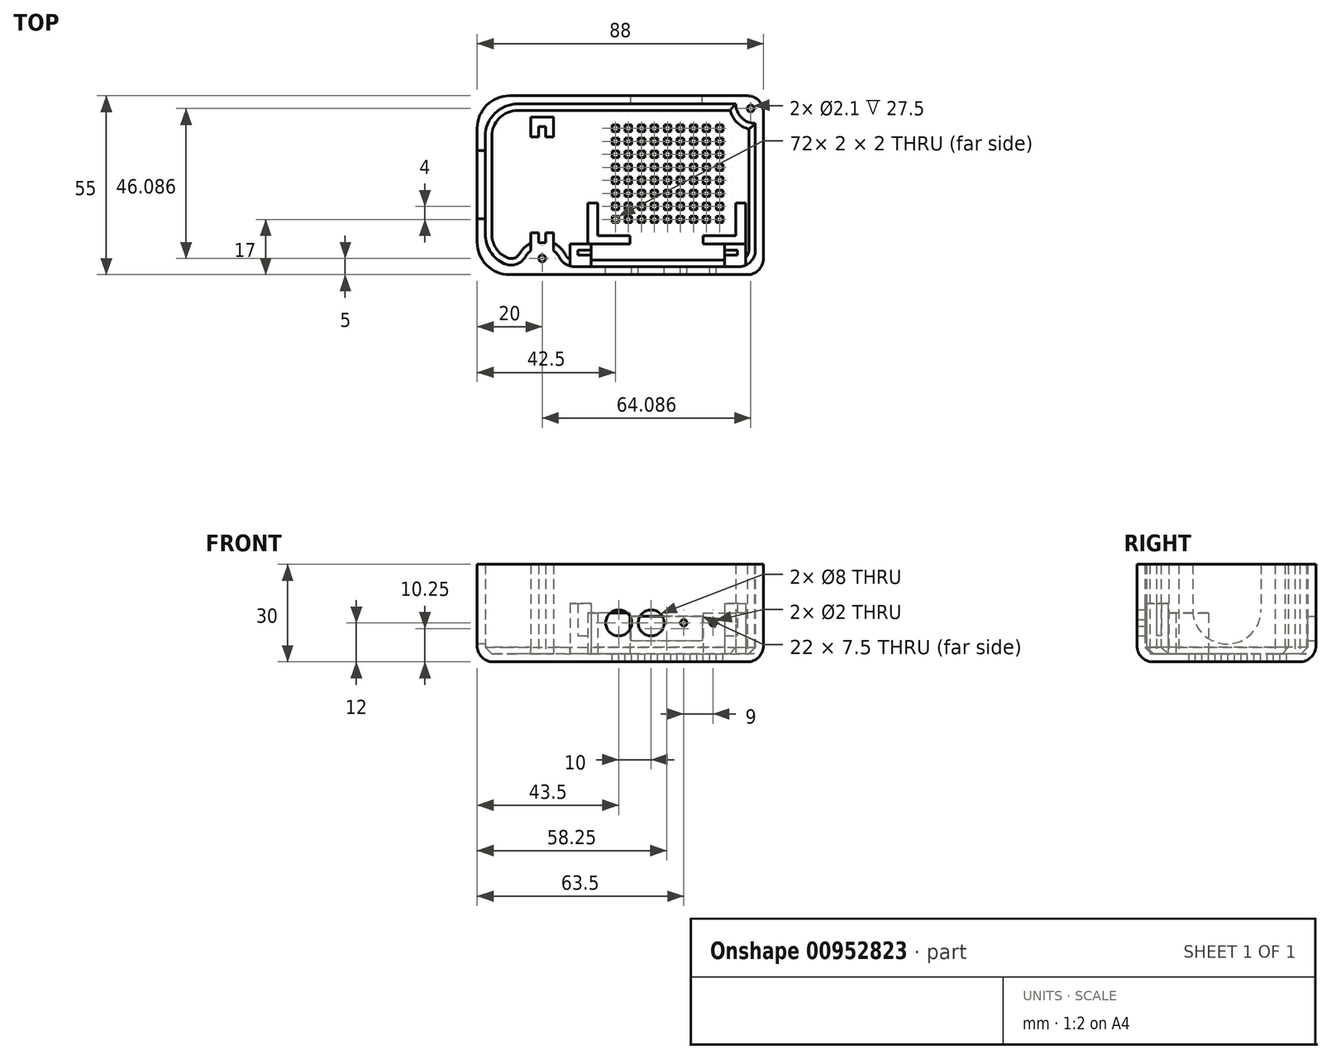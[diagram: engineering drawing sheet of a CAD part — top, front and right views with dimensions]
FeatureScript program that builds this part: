
annotation { "Feature Type Name" : "Feature", "Feature Type Description" : "" }
export const myFeature = defineFeature(function(context is Context, id is Id, definition is map)
    precondition{}
    {
        {
            var Q0;
            Q0=qCreatedBy(makeId("Top.planeOp"),FACE);
            var sketch = newSketch(context, id + "F0", { "sketchPlane" : qUnion([Q0])});
            skLineSegment(sketch, "E0", {"start": v(-88, 0) * mm, "end": v(0, 0) * mm});
            skLineSegment(sketch, "E1", {"start": v(0, 0) * mm, "end": v(0, -55) * mm});
            skLineSegment(sketch, "E2", {"start": v(0, -55) * mm, "end": v(-88, -55) * mm});
            skLineSegment(sketch, "E3", {"start": v(-88, -55) * mm, "end": v(-88, 0) * mm});
            skLineSegment(sketch, "E4", {"start": v(-85.5, -52.5) * mm, "end": v(-85.5, -2.5) * mm});
            skLineSegment(sketch, "E5", {"start": v(-71.5, -12.6) * mm, "end": v(-71.5, -6.5) * mm});
            skLineSegment(sketch, "E6", {"start": v(-64.5, -6.5) * mm, "end": v(-64.5, -12.6) * mm});
            skLineSegment(sketch, "E7", {"start": v(-64.5, -12.6) * mm, "end": v(-66.95, -12.6) * mm});
            skLineSegment(sketch, "E8", {"start": v(-66.95, -12.6) * mm, "end": v(-66.95, -9.5) * mm});
            skLineSegment(sketch, "E9", {"start": v(-66.95, -9.5) * mm, "end": v(-69.05, -9.5) * mm});
            skLineSegment(sketch, "E10", {"start": v(-69.05, -9.5) * mm, "end": v(-69.05, -12.6) * mm});
            skLineSegment(sketch, "E11", {"start": v(-69.05, -12.6) * mm, "end": v(-71.5, -12.6) * mm});
            skLineSegment(sketch, "E12", {"start": v(-93.85, -27.35) * mm, "end": v(11.82, -27.35) * mm, "construction": true});
            skLineSegment(sketch, "E13.MirrorCS", {"start": v(-69.05, -42.1) * mm, "end": v(-71.5, -42.1) * mm});
            skLineSegment(sketch, "E14.MirrorCS", {"start": v(-66.95, -42.1) * mm, "end": v(-66.95, -45.2) * mm});
            skLineSegment(sketch, "E15.MirrorCS", {"start": v(-71.5, -42.1) * mm, "end": v(-71.5, -47.63) * mm});
            skLineSegment(sketch, "E16.MirrorCS", {"start": v(-69.05, -45.2) * mm, "end": v(-69.05, -42.1) * mm});
            skLineSegment(sketch, "E17.MirrorCS", {"start": v(-66.95, -45.2) * mm, "end": v(-69.05, -45.2) * mm});
            skLineSegment(sketch, "E18.MirrorCS", {"start": v(-64.5, -42.1) * mm, "end": v(-66.95, -42.1) * mm});
            skLineSegment(sketch, "E19", {"start": v(-85.5, -52.5) * mm, "end": v(-2.5, -52.5) * mm});
            skLineSegment(sketch, "E20", {"start": v(-71.5, -6.5) * mm, "end": v(-64.5, -6.5) * mm});
            skArc(sketch, "E21", {"start": v(-8.5, -2.5) * mm, "mid": v(-6.74, -6.74) * mm, "end": v(-2.5, -8.5) * mm});
            skArc(sketch, "E22", {"start": v(-74, -52.5) * mm, "mid": v(-73.34, -49.76) * mm, "end": v(-71.5, -47.63) * mm});
            skLineSegment(sketch, "E23", {"start": v(-64.5, -47.82) * mm, "end": v(-64.5, -47.82) * mm});
            skLineSegment(sketch, "E24", {"start": v(-64.5, -47.82) * mm, "end": v(-64.5, -42.1) * mm});
            skArc(sketch, "E25", {"start": v(-64.5, -47.63) * mm, "mid": v(-62.66, -49.76) * mm, "end": v(-62, -52.5) * mm});
            skLineSegment(sketch, "E26", {"start": v(-8.5, -2.5) * mm, "end": v(-85.5, -2.5) * mm});
            skLineSegment(sketch, "E27", {"start": v(-2.5, -8.5) * mm, "end": v(-2.5, -52.5) * mm});
            skLineSegment(sketch, "E28", {"start": v(-68, -52.5) * mm, "end": v(-68, -38.94) * mm, "construction": true});
            skCircle(sketch, "E29", {"center": v(-68, -50) * mm, "radius": 1.05 * mm});
            skLineSegment(sketch, "E30", {"start": v(-2.5, -2.5) * mm, "end": v(-3.91, -3.91) * mm, "construction": true});
            skLineSegment(sketch, "E31", {"start": v(-3.91, -3.91) * mm, "end": v(-2.5, -5.33) * mm, "construction": true});
            skCircle(sketch, "E32", {"center": v(-3.91, -3.91) * mm, "radius": 1.05 * mm});
            skSolve(sketch);
        }
        {
            var Q0;
            Q0=qCreatedBy(makeId("Top.planeOp"),FACE);
            var sketch = newSketch(context, id + "F1", { "sketchPlane" : qUnion([Q0])});
            skPoint(sketch, "E33.middle", {"position": v(0, 0) * mm});
            skLineSegment(sketch, "E34.bottom", {"start": v(0, 0) * mm, "end": v(-88, 0) * mm});
            skLineSegment(sketch, "E34.top", {"start": v(0, -55) * mm, "end": v(-88, -55) * mm});
            skLineSegment(sketch, "E34.left", {"start": v(0, 0) * mm, "end": v(0, -55) * mm});
            skLineSegment(sketch, "E34.right", {"start": v(-88, 0) * mm, "end": v(-88, -55) * mm});
            skSolve(sketch);
        }
        {
            var Q0;
            Q0=qCreatedBy(makeId("Top.planeOp"),FACE);
            var sketch = newSketch(context, id + "F2", { "sketchPlane" : qUnion([Q0])});
            skLineSegment(sketch, "E35", {"start": v(-5.5, -33) * mm, "end": v(-8.5, -33) * mm});
            skLineSegment(sketch, "E36", {"start": v(-8.5, -33) * mm, "end": v(-8.5, -43) * mm});
            skLineSegment(sketch, "E37", {"start": v(-18.5, -43) * mm, "end": v(-8.5, -43) * mm});
            skLineSegment(sketch, "E38", {"start": v(-18.5, -43) * mm, "end": v(-18.5, -45.5) * mm});
            skLineSegment(sketch, "E39", {"start": v(-18.5, -45.5) * mm, "end": v(-5.5, -45.5) * mm});
            skLineSegment(sketch, "E40", {"start": v(-5.5, -45.5) * mm, "end": v(-5.5, -33) * mm});
            skLineSegment(sketch, "E41", {"start": v(-29.75, -52.22) * mm, "end": v(-29.75, 32.06) * mm, "construction": true});
            skLineSegment(sketch, "E42.MirrorCS", {"start": v(-54, -33) * mm, "end": v(-51, -33) * mm});
            skLineSegment(sketch, "E43.MirrorCS", {"start": v(-41, -43) * mm, "end": v(-41, -45.5) * mm});
            skLineSegment(sketch, "E44.MirrorCS", {"start": v(-51, -33) * mm, "end": v(-51, -43) * mm});
            skLineSegment(sketch, "E45.MirrorCS", {"start": v(-41, -45.5) * mm, "end": v(-54, -45.5) * mm});
            skLineSegment(sketch, "E46.MirrorCS", {"start": v(-54, -45.5) * mm, "end": v(-54, -33) * mm});
            skLineSegment(sketch, "E47.MirrorCS", {"start": v(-41, -43) * mm, "end": v(-51, -43) * mm});
            skSolve(sketch);
        }
        {
            var Q0;
            Q0=qCreatedBy(makeId("Top.planeOp"),FACE);
            var sketch = newSketch(context, id + "F3", { "sketchPlane" : qUnion([Q0])});
            skLineSegment(sketch, "E48", {"start": v(-32.5, -56.28) * mm, "end": v(-32.5, -44.7) * mm, "construction": true});
            skLineSegment(sketch, "E49", {"start": v(-12, -45.5) * mm, "end": v(-5.5, -45.5) * mm});
            skLineSegment(sketch, "E50", {"start": v(-12, -52.5) * mm, "end": v(-5.5, -52.5) * mm});
            skLineSegment(sketch, "E51", {"start": v(-12, -45.5) * mm, "end": v(-12, -52.5) * mm});
            skLineSegment(sketch, "E52.MirrorCS", {"start": v(-53, -45.5) * mm, "end": v(-53, -52.5) * mm});
            skLineSegment(sketch, "E53.MirrorCS", {"start": v(-53, -45.5) * mm, "end": v(-59.5, -45.5) * mm});
            skPoint(sketch, "E54", {"position": v(-5.5, -45.5) * mm});
            skPoint(sketch, "E55", {"position": v(-5.5, -52.5) * mm});
            skLineSegment(sketch, "E56", {"start": v(-5.5, -45.5) * mm, "end": v(-5.5, -52.5) * mm});
            skLineSegment(sketch, "E57", {"start": v(-5.5, -52.5) * mm, "end": v(-5.5, -52.5) * mm});
            skLineSegment(sketch, "E58.MirrorCS", {"start": v(-59.5, -45.5) * mm, "end": v(-59.5, -52.5) * mm});
            skLineSegment(sketch, "E59.MirrorCS", {"start": v(-53, -52.5) * mm, "end": v(-59.5, -52.5) * mm});
            skSolve(sketch);
        }
        {
            var Q0;
            Q0=qCreatedBy(makeId("Top.planeOp"),FACE);
            var sketch = newSketch(context, id + "F4", { "sketchPlane" : qUnion([Q0])});
            skLineSegment(sketch, "E60", {"start": v(-12, -52.5) * mm, "end": v(-12, -49) * mm});
            skLineSegment(sketch, "E61", {"start": v(-12, -49) * mm, "end": v(-8, -49) * mm});
            skLineSegment(sketch, "E62", {"start": v(-8, -49) * mm, "end": v(-8, -47.5) * mm});
            skLineSegment(sketch, "E63", {"start": v(-8, -47.5) * mm, "end": v(-12, -47.5) * mm});
            skLineSegment(sketch, "E64", {"start": v(-12, -47.5) * mm, "end": v(-12, -45.5) * mm});
            skLineSegment(sketch, "E65", {"start": v(-32.5, -55) * mm, "end": v(-32.5, -43.43) * mm, "construction": true});
            skLineSegment(sketch, "E66", {"start": v(-12, -45.5) * mm, "end": v(-5.5, -45.5) * mm});
            skLineSegment(sketch, "E67.MirrorCS", {"start": v(-57, -49) * mm, "end": v(-57, -47.5) * mm});
            skLineSegment(sketch, "E68.MirrorCS", {"start": v(-53, -52.5) * mm, "end": v(-53, -49) * mm});
            skLineSegment(sketch, "E69.MirrorCS", {"start": v(-57, -47.5) * mm, "end": v(-53, -47.5) * mm});
            skLineSegment(sketch, "E70.MirrorCS", {"start": v(-59.5, -52.5) * mm, "end": v(-53, -52.5) * mm});
            skLineSegment(sketch, "E71.MirrorCS", {"start": v(-53, -47.5) * mm, "end": v(-53, -45.5) * mm});
            skLineSegment(sketch, "E72.MirrorCS", {"start": v(-53, -49) * mm, "end": v(-57, -49) * mm});
            skLineSegment(sketch, "E73.MirrorCS", {"start": v(-53, -45.5) * mm, "end": v(-59.5, -45.5) * mm});
            skLineSegment(sketch, "E74", {"start": v(-5.5, -45.5) * mm, "end": v(-5.5, -52.5) * mm});
            skLineSegment(sketch, "E75", {"start": v(-5.5, -52.5) * mm, "end": v(-5.5, -52.5) * mm});
            skLineSegment(sketch, "E76", {"start": v(-5.5, -52.5) * mm, "end": v(-12, -52.5) * mm});
            skLineSegment(sketch, "E77.MirrorCS", {"start": v(21.5, -55) * mm, "end": v(21.5, -43.43) * mm, "construction": true});
            skLineSegment(sketch, "E78.MirrorCS", {"start": v(-59.5, -45.5) * mm, "end": v(-59.5, -52.5) * mm});
            skSolve(sketch);
        }
        {
            var Q0;
            Q0=makeQuery(id+"F0.imprint","IMPRINT",FACE,{"disambiguationData":[TD([[makeQuery(id+"F0.imprint","IMPRINT",EDGE,{"derivedFrom":sQuery(id+"F0.wireOp",EDGE,"E0")}),-1.0]])]});
            var Q1;
            Q1=makeQuery(id+"F0.imprint","IMPRINT",FACE,{"disambiguationData":[TD([[makeQuery(id+"F0.imprint","IMPRINT",EDGE,{"derivedFrom":sQuery(id+"F0.wireOp",EDGE,"E13.MirrorCS")}),1.0]])]});
            var Q2;
            Q2=makeQuery(id+"F0.imprint","IMPRINT",FACE,{"disambiguationData":[TD([[makeQuery(id+"F0.imprint","IMPRINT",EDGE,{"derivedFrom":sQuery(id+"F0.wireOp",EDGE,"E5")}),-1.0]])]});
            extrude(context, id + "F5", {"entities" : qUnion([Q0, Q1, Q2]), "depth" : 30 * mm, "offsetDistance" : 25 * mm});
        }
        {
            var Q0;
            Q0 = qSketchRegion(id + "F2", true);
            extrude(context, id + "F6", {"entities" : qUnion([Q0]), "depth" : 15 * mm, "offsetDistance" : 25 * mm});
        }
        {
            var Q0;
            Q0 = qSketchRegion(id + "F3", true);
            extrude(context, id + "F7", {"entities" : qUnion([Q0]), "operationType" : NewBodyOperationType.ADD, "depth" : 8 * mm, "offsetDistance" : 25 * mm});
        }
        {
            var Q0;
            Q0 = qSketchRegion(id + "F4", true);
            extrude(context, id + "F8", {"entities" : qUnion([Q0]), "operationType" : NewBodyOperationType.ADD, "depth" : 18 * mm, "offsetDistance" : 25 * mm});
        }
        {
            var Q0;
            Q0 = qSketchRegion(id + "F1", true);
            extrude(context, id + "F9", {"entities" : qUnion([Q0]), "depth" : 2.5 * mm, "offsetDistance" : 25 * mm});
        }
        {
            var Q0;
            Q0=makeQuery(id+"F5.opExtrude","SWEPT_BODY",BODY,{"disambiguationData":[OSD([sQuery(id+"F0.wireOp",EDGE,"E0"),sQuery(id+"F0.wireOp",EDGE,"E1"),sQuery(id+"F0.wireOp",EDGE,"E2"),sQuery(id+"F0.wireOp",EDGE,"E3"),sQuery(id+"F0.wireOp",EDGE,"UuoHDoxM-e8rz-IagH-wuba-yFCC0wOmhfrt"),sQuery(id+"F0.wireOp",EDGE,"E4"),sQuery(id+"F0.wireOp",EDGE,"E5"),sQuery(id+"F0.wireOp",EDGE,"E6"),sQuery(id+"F0.wireOp",EDGE,"E7"),sQuery(id+"F0.wireOp",EDGE,"E8"),sQuery(id+"F0.wireOp",EDGE,"E9"),sQuery(id+"F0.wireOp",EDGE,"E10"),sQuery(id+"F0.wireOp",EDGE,"E11"),sQuery(id+"F0.wireOp",EDGE,"c786309d-101e-4053-9150-d0af641cc12e"),sQuery(id+"F0.wireOp",EDGE,"E19"),sQuery(id+"F0.wireOp",EDGE,"HcqVvm8B-6W9z-mqu9-0GbS-zFuDXKySd18V")])]});
            var Q1;
            Q1=makeQuery(id+"F5.opExtrude","SWEPT_BODY",BODY,{"disambiguationData":[OSD([sQuery(id+"F0.wireOp",EDGE,"E13.MirrorCS"),sQuery(id+"F0.wireOp",EDGE,"E14.MirrorCS"),sQuery(id+"F0.wireOp",EDGE,"E15.MirrorCS"),sQuery(id+"F0.wireOp",EDGE,"064b8b4c-f276-4261-8800-d9a24fd23e0e3.MirrorCS"),sQuery(id+"F0.wireOp",EDGE,"E16.MirrorCS"),sQuery(id+"F0.wireOp",EDGE,"E17.MirrorCS"),sQuery(id+"F0.wireOp",EDGE,"E18.MirrorCS"),sQuery(id+"F0.wireOp",EDGE,"gorcFAZ2-i92h-ynGc-5GPt-G5OjvUxhf4RJ")])]});
            var Q2;
            Q2=makeQuery(id+"F6.opExtrude","SWEPT_BODY",BODY,{"disambiguationData":[OSD([sQuery(id+"F2.wireOp",EDGE,"fb9ec073-7efa-4419-bfd9-468364ba8700"),sQuery(id+"F2.wireOp",EDGE,"ed1e150d-128d-4553-bff4-cb28458386a2"),sQuery(id+"F2.wireOp",EDGE,"0a0392a0-6fd0-4df2-8425-dfe9aab30372"),sQuery(id+"F2.wireOp",EDGE,"c3ed98f8-111d-4dfb-8951-0a7b6b337b95"),sQuery(id+"F2.wireOp",EDGE,"ekVp80hc-O6ig-nOgL-KVfI-wofW4DGdbD3E"),sQuery(id+"F2.wireOp",EDGE,"EOFYb0tf-Urno-pUMQ-HgLK-OjDsxmRxz7sO")])]});
            var Q3;
            Q3=makeQuery(id+"F6.opExtrude","SWEPT_BODY",BODY,{"disambiguationData":[OSD([sQuery(id+"F2.wireOp",EDGE,"E35"),sQuery(id+"F2.wireOp",EDGE,"E36"),sQuery(id+"F2.wireOp",EDGE,"E37"),sQuery(id+"F2.wireOp",EDGE,"E38"),sQuery(id+"F2.wireOp",EDGE,"E39"),sQuery(id+"F2.wireOp",EDGE,"E40")])]});
            var Q4;
            Q4=makeQuery(id+"F9.opExtrude","SWEPT_BODY",BODY,{"disambiguationData":[OSD([sQuery(id+"F1.wireOp",EDGE,"E34.bottom"),sQuery(id+"F1.wireOp",EDGE,"E34.top"),sQuery(id+"F1.wireOp",EDGE,"E34.left"),sQuery(id+"F1.wireOp",EDGE,"E34.right")])]});
            var Q5;
            Q5=makeQuery(id+"F8.opExtrude","SWEPT_BODY",BODY,{"disambiguationData":[OSD([sQuery(id+"F4.wireOp",EDGE,"E60"),sQuery(id+"F4.wireOp",EDGE,"E61"),sQuery(id+"F4.wireOp",EDGE,"E62"),sQuery(id+"F4.wireOp",EDGE,"E63"),sQuery(id+"F4.wireOp",EDGE,"E64"),sQuery(id+"F4.wireOp",EDGE,"E66"),sQuery(id+"F4.wireOp",EDGE,"E74"),sQuery(id+"F4.wireOp",EDGE,"E76")])]});
            var Q6;
            Q6=makeQuery(id+"F8.opExtrude","SWEPT_BODY",BODY,{"disambiguationData":[OSD([sQuery(id+"F4.wireOp",EDGE,"E67.MirrorCS"),sQuery(id+"F4.wireOp",EDGE,"E68.MirrorCS"),sQuery(id+"F4.wireOp",EDGE,"E69.MirrorCS"),sQuery(id+"F4.wireOp",EDGE,"E70.MirrorCS"),sQuery(id+"F4.wireOp",EDGE,"E71.MirrorCS"),sQuery(id+"F4.wireOp",EDGE,"E72.MirrorCS"),sQuery(id+"F4.wireOp",EDGE,"E73.MirrorCS"),sQuery(id+"F4.wireOp",EDGE,"E78.MirrorCS")])]});
            var Q7;
            Q7=makeQuery(id+"F7.opExtrude","SWEPT_BODY",BODY,{"disambiguationData":[OSD([sQuery(id+"F3.wireOp",EDGE,"E49"),sQuery(id+"F3.wireOp",EDGE,"E50"),sQuery(id+"F3.wireOp",EDGE,"E51"),sQuery(id+"F3.wireOp",EDGE,"E56")])]});
            var Q8;
            Q8=makeQuery(id+"F7.opExtrude","SWEPT_BODY",BODY,{"disambiguationData":[OSD([sQuery(id+"F3.wireOp",EDGE,"E52.MirrorCS"),sQuery(id+"F3.wireOp",EDGE,"E53.MirrorCS"),sQuery(id+"F3.wireOp",EDGE,"E58.MirrorCS"),sQuery(id+"F3.wireOp",EDGE,"E59.MirrorCS")])]});
            var Q9;
            Q9=makeQuery(id+"F6.opExtrude","SWEPT_BODY",BODY,{"disambiguationData":[OSD([sQuery(id+"F2.wireOp",EDGE,"E42.MirrorCS"),sQuery(id+"F2.wireOp",EDGE,"E43.MirrorCS"),sQuery(id+"F2.wireOp",EDGE,"E44.MirrorCS"),sQuery(id+"F2.wireOp",EDGE,"E45.MirrorCS"),sQuery(id+"F2.wireOp",EDGE,"E46.MirrorCS"),sQuery(id+"F2.wireOp",EDGE,"E47.MirrorCS")])]});
            booleanBodies(context, id + "F10", {"operationType" : BooleanOperationType.UNION, "tools" : qUnion([Q0, Q1, Q2, Q3, Q4, Q5, Q6, Q7, Q8, Q9])});
        }
        {
            var Q0;
            Q0=makeQuery(id+"F5.opExtrude","SWEPT_FACE",FACE,{"disambiguationData":[OSD([sQuery(id+"F0.wireOp",EDGE,"E3")])]});
            var sketch = newSketch(context, id + "F11", { "sketchPlane" : qUnion([Q0])});
            skLineSegment(sketch, "E79", {"start": v(27.35, 32.52) * mm, "end": v(27.35, -6.46) * mm, "construction": true});
            skLineSegment(sketch, "E80", {"start": v(37.85, 30) * mm, "end": v(37.85, 16) * mm});
            skLineSegment(sketch, "E81", {"start": v(37.85, 16) * mm, "end": v(27.35, 16) * mm, "construction": true});
            skArc(sketch, "E82", {"start": v(37.85, 16) * mm, "mid": v(34.77, 8.58) * mm, "end": v(27.35, 5.5) * mm});
            skLineSegment(sketch, "E83.MirrorCS", {"start": v(16.85, 30) * mm, "end": v(16.85, 16) * mm});
            skArc(sketch, "E84.MirrorCS", {"start": v(16.85, 16) * mm, "mid": v(19.93, 8.58) * mm, "end": v(27.35, 5.5) * mm});
            skLineSegment(sketch, "E85", {"start": v(16.85, 30) * mm, "end": v(37.85, 30) * mm});
            skSolve(sketch);
        }
        {
            var Q0;
            Q0=makeQuery(id+"F11.imprint","IMPRINT",FACE,{"disambiguationData":[TD([[makeQuery(id+"F11.imprint","IMPRINT",EDGE,{"derivedFrom":sQuery(id+"F11.wireOp",EDGE,"E80")}),-1.0]])]});
            extrude(context, id + "F12", {"entities" : qUnion([Q0]), "operationType" : NewBodyOperationType.REMOVE, "oppositeDirection" : true, "depth" : 4 * mm, "offsetDistance" : 25 * mm});
        }
        {
            var Q0;
            Q0=makeQuery(id+"F5.opExtrude","SWEPT_EDGE",EDGE,{"disambiguationData":[OSD([sQuery(id+"F0.wireOp",EDGE,"E2"),sQuery(id+"F0.wireOp",EDGE,"E3")])]});
            var Q1;
            Q1=makeQuery(id+"F5.opExtrude","SWEPT_EDGE",EDGE,{"disambiguationData":[OSD([sQuery(id+"F0.wireOp",EDGE,"E0"),sQuery(id+"F0.wireOp",EDGE,"E3")])]});
            var Q2;
            Q2=makeQuery(id+"F5.opExtrude","SWEPT_EDGE",EDGE,{"disambiguationData":[OSD([sQuery(id+"F0.wireOp",EDGE,"E4"),sQuery(id+"F0.wireOp",EDGE,"E19")])]});
            var Q3;
            Q3=makeQuery(id+"F5.opExtrude","SWEPT_EDGE",EDGE,{"disambiguationData":[OSD([sQuery(id+"F0.wireOp",EDGE,"UuoHDoxM-e8rz-IagH-wuba-yFCC0wOmhfrt"),sQuery(id+"F0.wireOp",EDGE,"E4")])]});
            fillet(context, id + "F13", {"entities" : qUnion([Q0, Q1, Q2, Q3]), "radius" : 10 * mm, "tangentPropagation" : true, "allowEdgeOverflow" : false});
        }
        {
            var Q0;
            Q0=makeQuery(id+"F5.opExtrude","SWEPT_EDGE",EDGE,{"disambiguationData":[OSD([sQuery(id+"F0.wireOp",EDGE,"E1"),sQuery(id+"F0.wireOp",EDGE,"E2")])]});
            var Q1;
            Q1=makeQuery(id+"F5.opExtrude","SWEPT_EDGE",EDGE,{"disambiguationData":[OSD([sQuery(id+"F0.wireOp",EDGE,"E0"),sQuery(id+"F0.wireOp",EDGE,"E1")])]});
            var Q2;
            Q2=makeQuery(id+"F5.opExtrude","SWEPT_EDGE",EDGE,{"disambiguationData":[OSD([sQuery(id+"F0.wireOp",EDGE,"c786309d-101e-4053-9150-d0af641cc12e"),sQuery(id+"F0.wireOp",EDGE,"HcqVvm8B-6W9z-mqu9-0GbS-zFuDXKySd18V")])]});
            var Q3;
            Q3=makeQuery(id+"F5.opExtrude","SWEPT_EDGE",EDGE,{"disambiguationData":[OSD([sQuery(id+"F0.wireOp",EDGE,"E19"),sQuery(id+"F0.wireOp",EDGE,"HcqVvm8B-6W9z-mqu9-0GbS-zFuDXKySd18V")])]});
            fillet(context, id + "F14", {"entities" : qUnion([Q0, Q1, Q2, Q3]), "radius" : 5 * mm, "tangentPropagation" : true, "allowEdgeOverflow" : false});
        }
        {
            var Q0;
            Q0=makeQuery(id+"F10.opBoolean","MERGE",FACE,{"derivedFrom":[makeQuery(id+"F5.opExtrude","CAP_FACE",FACE,{"disambiguationData":[OSD([sQuery(id+"F0.wireOp",EDGE,"E0"),sQuery(id+"F0.wireOp",EDGE,"E1"),sQuery(id+"F0.wireOp",EDGE,"E2"),sQuery(id+"F0.wireOp",EDGE,"E3"),sQuery(id+"F0.wireOp",EDGE,"E4"),sQuery(id+"F0.wireOp",EDGE,"E13.MirrorCS"),sQuery(id+"F0.wireOp",EDGE,"E14.MirrorCS"),sQuery(id+"F0.wireOp",EDGE,"E15.MirrorCS"),sQuery(id+"F0.wireOp",EDGE,"E16.MirrorCS"),sQuery(id+"F0.wireOp",EDGE,"E17.MirrorCS"),sQuery(id+"F0.wireOp",EDGE,"E18.MirrorCS"),sQuery(id+"F0.wireOp",EDGE,"E19"),sQuery(id+"F0.wireOp",EDGE,"E21"),sQuery(id+"F0.wireOp",EDGE,"E22"),sQuery(id+"F0.wireOp",EDGE,"E24"),sQuery(id+"F0.wireOp",EDGE,"E25"),sQuery(id+"F0.wireOp",EDGE,"E26"),sQuery(id+"F0.wireOp",EDGE,"E27"),sQuery(id+"F0.wireOp",EDGE,"E29"),sQuery(id+"F0.wireOp",EDGE,"E32")])],"isStart":true}),makeQuery(id+"F5.opExtrude","CAP_FACE",FACE,{"disambiguationData":[OSD([sQuery(id+"F0.wireOp",EDGE,"E5"),sQuery(id+"F0.wireOp",EDGE,"E6"),sQuery(id+"F0.wireOp",EDGE,"E7"),sQuery(id+"F0.wireOp",EDGE,"E8"),sQuery(id+"F0.wireOp",EDGE,"E9"),sQuery(id+"F0.wireOp",EDGE,"E10"),sQuery(id+"F0.wireOp",EDGE,"E11"),sQuery(id+"F0.wireOp",EDGE,"E20")])],"isStart":true}),makeQuery(id+"F6.opExtrude","CAP_FACE",FACE,{"disambiguationData":[OSD([sQuery(id+"F2.wireOp",EDGE,"fb9ec073-7efa-4419-bfd9-468364ba8700"),sQuery(id+"F2.wireOp",EDGE,"ed1e150d-128d-4553-bff4-cb28458386a2"),sQuery(id+"F2.wireOp",EDGE,"0a0392a0-6fd0-4df2-8425-dfe9aab30372"),sQuery(id+"F2.wireOp",EDGE,"c3ed98f8-111d-4dfb-8951-0a7b6b337b95"),sQuery(id+"F2.wireOp",EDGE,"ekVp80hc-O6ig-nOgL-KVfI-wofW4DGdbD3E"),sQuery(id+"F2.wireOp",EDGE,"EOFYb0tf-Urno-pUMQ-HgLK-OjDsxmRxz7sO")])],"isStart":true}),makeQuery(id+"F6.opExtrude","CAP_FACE",FACE,{"disambiguationData":[OSD([sQuery(id+"F2.wireOp",EDGE,"E35"),sQuery(id+"F2.wireOp",EDGE,"E36"),sQuery(id+"F2.wireOp",EDGE,"E37"),sQuery(id+"F2.wireOp",EDGE,"E38"),sQuery(id+"F2.wireOp",EDGE,"E39"),sQuery(id+"F2.wireOp",EDGE,"E40")])],"isStart":true}),makeQuery(id+"F9.opExtrude","CAP_FACE",FACE,{"disambiguationData":[OSD([sQuery(id+"F1.wireOp",EDGE,"E34.bottom"),sQuery(id+"F1.wireOp",EDGE,"E34.top"),sQuery(id+"F1.wireOp",EDGE,"E34.left"),sQuery(id+"F1.wireOp",EDGE,"E34.right")])],"isStart":true})]});
            fillet(context, id + "F15", {"entities" : qUnion([Q0]), "radius" : 5 * mm, "tangentPropagation" : true, "allowEdgeOverflow" : false});
        }
        {
            var Q0;
            Q0=makeQuery(id+"F10.opBoolean","INTERSECT",EDGE,{"derivedFrom":[makeQuery(id+"F5.opExtrude","SWEPT_FACE",FACE,{"disambiguationData":[OSD([sQuery(id+"F0.wireOp",EDGE,"E21")])]}),makeQuery(id+"F9.opExtrude","CAP_FACE",FACE,{"disambiguationData":[OSD([sQuery(id+"F1.wireOp",EDGE,"E34.bottom"),sQuery(id+"F1.wireOp",EDGE,"E34.top"),sQuery(id+"F1.wireOp",EDGE,"E34.left"),sQuery(id+"F1.wireOp",EDGE,"E34.right")])],"isStart":false})]});
            var Q1;
            Q1=makeQuery(id+"F10.opBoolean","INTERSECT",EDGE,{"derivedFrom":[makeQuery(id+"F5.opExtrude","SWEPT_FACE",FACE,{"disambiguationData":[OSD([sQuery(id+"F0.wireOp",EDGE,"E27")])]}),makeQuery(id+"F9.opExtrude","CAP_FACE",FACE,{"disambiguationData":[OSD([sQuery(id+"F1.wireOp",EDGE,"E34.bottom"),sQuery(id+"F1.wireOp",EDGE,"E34.top"),sQuery(id+"F1.wireOp",EDGE,"E34.left"),sQuery(id+"F1.wireOp",EDGE,"E34.right")])],"isStart":false})]});
            var Q2;
            {var subQ0=sQuery(id+"F0.wireOp",EDGE,"E19");Q2=makeQuery(id+"F10.opBoolean","INTERSECT",EDGE,{"disambiguationData":[OD(2.0)],"derivedFrom":[makeQuery(id+"F5.opExtrude","SWEPT_FACE",FACE,{"disambiguationData":[OSD([subQ0]),TDD([makeQuery(id+"F0.imprint","IMPRINT",EDGE,{"disambiguationData":[TD([[makeQuery(id+"F0.imprint","INTERSECT",VERTEX,{"derivedFrom":[subQ0,sQuery(id+"F0.wireOp",EDGE,"E27")]}),1.0]])],"derivedFrom":subQ0})])]}),makeQuery(id+"F9.opExtrude","CAP_FACE",FACE,{"disambiguationData":[OSD([sQuery(id+"F1.wireOp",EDGE,"E34.bottom"),sQuery(id+"F1.wireOp",EDGE,"E34.top"),sQuery(id+"F1.wireOp",EDGE,"E34.left"),sQuery(id+"F1.wireOp",EDGE,"E34.right")])],"isStart":false})]});}
            var Q3;
            {var subQ0=sQuery(id+"F0.wireOp",EDGE,"E25");var subQ3=sQuery(id+"F0.wireOp",EDGE,"E19");var subQ4=sQuery(id+"F0.wireOp",EDGE,"E4");Q3=makeQuery(id+"F14.opFillet","BLEND_EDGE",EDGE,{"blendedFrom":[makeQuery(id+"F5.opExtrude","SWEPT_EDGE",EDGE,{"disambiguationData":[OSD([subQ3,subQ0])]}),makeQuery(id+"F10.opBoolean","SPLIT",FACE,{"disambiguationData":[TD([makeQuery(id+"F5.opExtrude","SWEPT_FACE",FACE,{"disambiguationData":[OSD([subQ4])]})])],"derivedFrom":makeQuery(id+"F9.opExtrude","CAP_FACE",FACE,{"disambiguationData":[OSD([sQuery(id+"F1.wireOp",EDGE,"E34.bottom"),sQuery(id+"F1.wireOp",EDGE,"E34.top"),sQuery(id+"F1.wireOp",EDGE,"E34.left"),sQuery(id+"F1.wireOp",EDGE,"E34.right")])],"isStart":false})})],"blendedInto":[makeQuery(id+"F10.opBoolean","SPLIT",FACE,{"disambiguationData":[TD([makeQuery(id+"F5.opExtrude","SWEPT_FACE",FACE,{"disambiguationData":[OSD([subQ4])]})])],"derivedFrom":makeQuery(id+"F9.opExtrude","CAP_FACE",FACE,{"disambiguationData":[OSD([sQuery(id+"F1.wireOp",EDGE,"E34.bottom"),sQuery(id+"F1.wireOp",EDGE,"E34.top"),sQuery(id+"F1.wireOp",EDGE,"E34.left"),sQuery(id+"F1.wireOp",EDGE,"E34.right")])],"isStart":false})})]});}
            var Q4;
            {var subQ4=sQuery(id+"F0.wireOp",EDGE,"E4");var subQ5=sQuery(id+"F0.wireOp",EDGE,"E26");Q4=makeQuery(id+"F13.opFillet","BLEND_EDGE",EDGE,{"blendedFrom":[makeQuery(id+"F5.opExtrude","SWEPT_EDGE",EDGE,{"disambiguationData":[OSD([subQ4,subQ5])]}),makeQuery(id+"F10.opBoolean","SPLIT",FACE,{"disambiguationData":[TD([makeQuery(id+"F5.opExtrude","SWEPT_FACE",FACE,{"disambiguationData":[OSD([subQ4])]})])],"derivedFrom":makeQuery(id+"F9.opExtrude","CAP_FACE",FACE,{"disambiguationData":[OSD([sQuery(id+"F1.wireOp",EDGE,"E34.bottom"),sQuery(id+"F1.wireOp",EDGE,"E34.top"),sQuery(id+"F1.wireOp",EDGE,"E34.left"),sQuery(id+"F1.wireOp",EDGE,"E34.right")])],"isStart":false})})],"blendedInto":[makeQuery(id+"F10.opBoolean","SPLIT",FACE,{"disambiguationData":[TD([makeQuery(id+"F5.opExtrude","SWEPT_FACE",FACE,{"disambiguationData":[OSD([subQ4])]})])],"derivedFrom":makeQuery(id+"F9.opExtrude","CAP_FACE",FACE,{"disambiguationData":[OSD([sQuery(id+"F1.wireOp",EDGE,"E34.bottom"),sQuery(id+"F1.wireOp",EDGE,"E34.top"),sQuery(id+"F1.wireOp",EDGE,"E34.left"),sQuery(id+"F1.wireOp",EDGE,"E34.right")])],"isStart":false})})]});}
            chamfer(context, id + "F16", {"entities" : qUnion([Q0, Q1, Q2, Q3, Q4]), "width" : 2 * mm, "tangentPropagation" : true});
        }
        {
            var Q0;
            {var subQ0=sQuery(id+"F0.wireOp",EDGE,"E19");Q0=makeQuery(id+"F5.opExtrude","SWEPT_FACE",FACE,{"disambiguationData":[OSD([subQ0]),TDD([makeQuery(id+"F0.imprint","IMPRINT",EDGE,{"disambiguationData":[TD([[makeQuery(id+"F0.imprint","INTERSECT",VERTEX,{"derivedFrom":[subQ0,sQuery(id+"F0.wireOp",EDGE,"E27")]}),1.0]])],"derivedFrom":subQ0})])]});}
            var sketch = newSketch(context, id + "F17", { "sketchPlane" : qUnion([Q0])});
            skLineSegment(sketch, "E86", {"start": v(32.5, 34.22) * mm, "end": v(32.5, -5.1) * mm, "construction": true});
            skLineSegment(sketch, "E87", {"start": v(7.5, 12) * mm, "end": v(58.2, 12) * mm, "construction": true});
            skCircle(sketch, "E88", {"center": v(34.5, 12) * mm, "radius": 4 * mm});
            skCircle(sketch, "E89", {"center": v(44.5, 12) * mm, "radius": 4 * mm});
            skLineSegment(sketch, "E90", {"start": v(56.5, 33.3) * mm, "end": v(56.5, -4.71) * mm});
            skCircle(sketch, "E91", {"center": v(24.5, 12) * mm, "radius": 1 * mm});
            skCircle(sketch, "E92", {"center": v(15.5, 12) * mm, "radius": 1 * mm});
            skSolve(sketch);
        }
        {
            var Q0;
            Q0 = qSketchRegion(id + "F17", true);
            extrude(context, id + "F18", {"entities" : qUnion([Q0]), "operationType" : NewBodyOperationType.REMOVE, "oppositeDirection" : true, "depth" : 25 * mm, "offsetDistance" : 25 * mm});
        }
        {
            var Q0;
            Q0=makeQuery(id+"F5.opExtrude","SWEPT_FACE",FACE,{"disambiguationData":[OSD([sQuery(id+"F0.wireOp",EDGE,"E0")])]});
            var sketch = newSketch(context, id + "F19", { "sketchPlane" : qUnion([Q0])});
            skLineSegment(sketch, "E93", {"start": v(29.75, 35.68) * mm, "end": v(29.75, -9.59) * mm, "construction": true});
            skLineSegment(sketch, "E94.bottom", {"start": v(40.75, 14) * mm, "end": v(18.75, 14) * mm});
            skLineSegment(sketch, "E94.top", {"start": v(40.75, 6.5) * mm, "end": v(18.75, 6.5) * mm});
            skLineSegment(sketch, "E94.left", {"start": v(40.75, 14) * mm, "end": v(40.75, 6.5) * mm});
            skLineSegment(sketch, "E94.right", {"start": v(18.75, 14) * mm, "end": v(18.75, 6.5) * mm});
            skPoint(sketch, "E94.middle", {"position": v(29.75, 10.25) * mm});
            skSolve(sketch);
        }
        {
            var Q0;
            Q0 = qSketchRegion(id + "F19", true);
            extrude(context, id + "F20", {"entities" : qUnion([Q0]), "operationType" : NewBodyOperationType.REMOVE, "oppositeDirection" : true, "depth" : 25 * mm, "offsetDistance" : 25 * mm});
        }
        {
            var Q0;
            {var subQ4=sQuery(id+"F0.wireOp",EDGE,"E4");Q0=makeQuery(id+"F10.opBoolean","SPLIT",FACE,{"disambiguationData":[TD([makeQuery(id+"F5.opExtrude","SWEPT_FACE",FACE,{"disambiguationData":[OSD([subQ4])]})])],"derivedFrom":makeQuery(id+"F9.opExtrude","CAP_FACE",FACE,{"disambiguationData":[OSD([sQuery(id+"F1.wireOp",EDGE,"E34.bottom"),sQuery(id+"F1.wireOp",EDGE,"E34.top"),sQuery(id+"F1.wireOp",EDGE,"E34.left"),sQuery(id+"F1.wireOp",EDGE,"E34.right")])],"isStart":false})});}
            var sketch = newSketch(context, id + "F21", { "sketchPlane" : qUnion([Q0])});
            skLineSegment(sketch, "E95.bottom", {"start": v(-14.5, -37) * mm, "end": v(-12.5, -37) * mm});
            skLineSegment(sketch, "E95.top", {"start": v(-14.5, -39) * mm, "end": v(-12.5, -39) * mm});
            skLineSegment(sketch, "E95.left", {"start": v(-14.5, -37) * mm, "end": v(-14.5, -39) * mm});
            skLineSegment(sketch, "E95.right", {"start": v(-12.5, -37) * mm, "end": v(-12.5, -39) * mm});
            skPoint(sketch, "E95.middle", {"position": v(-13.5, -38) * mm});
            skLineSegment(sketch, "E96.0.1.0", {"start": v(-14.5, -33) * mm, "end": v(-12.5, -33) * mm});
            skLineSegment(sketch, "E96.0.1.1", {"start": v(-12.5, -33) * mm, "end": v(-12.5, -35) * mm});
            skPoint(sketch, "E96.0.1.2", {"position": v(-13.5, -34) * mm});
            skLineSegment(sketch, "E96.0.1.3", {"start": v(-14.5, -35) * mm, "end": v(-12.5, -35) * mm});
            skLineSegment(sketch, "E96.0.1.4", {"start": v(-14.5, -33) * mm, "end": v(-14.5, -35) * mm});
            skLineSegment(sketch, "E96.0.2.0", {"start": v(-14.5, -29) * mm, "end": v(-12.5, -29) * mm});
            skLineSegment(sketch, "E96.0.2.1", {"start": v(-12.5, -29) * mm, "end": v(-12.5, -31) * mm});
            skPoint(sketch, "E96.0.2.2", {"position": v(-13.5, -30) * mm});
            skLineSegment(sketch, "E96.0.2.3", {"start": v(-14.5, -31) * mm, "end": v(-12.5, -31) * mm});
            skLineSegment(sketch, "E96.0.2.4", {"start": v(-14.5, -29) * mm, "end": v(-14.5, -31) * mm});
            skLineSegment(sketch, "E96.0.3.0", {"start": v(-14.5, -25) * mm, "end": v(-12.5, -25) * mm});
            skLineSegment(sketch, "E96.0.3.1", {"start": v(-12.5, -25) * mm, "end": v(-12.5, -27) * mm});
            skPoint(sketch, "E96.0.3.2", {"position": v(-13.5, -26) * mm});
            skLineSegment(sketch, "E96.0.3.3", {"start": v(-14.5, -27) * mm, "end": v(-12.5, -27) * mm});
            skLineSegment(sketch, "E96.0.3.4", {"start": v(-14.5, -25) * mm, "end": v(-14.5, -27) * mm});
            skLineSegment(sketch, "E96.0.4.0", {"start": v(-14.5, -21) * mm, "end": v(-12.5, -21) * mm});
            skLineSegment(sketch, "E96.0.4.1", {"start": v(-12.5, -21) * mm, "end": v(-12.5, -23) * mm});
            skPoint(sketch, "E96.0.4.2", {"position": v(-13.5, -22) * mm});
            skLineSegment(sketch, "E96.0.4.3", {"start": v(-14.5, -23) * mm, "end": v(-12.5, -23) * mm});
            skLineSegment(sketch, "E96.0.4.4", {"start": v(-14.5, -21) * mm, "end": v(-14.5, -23) * mm});
            skLineSegment(sketch, "E96.0.5.0", {"start": v(-14.5, -17) * mm, "end": v(-12.5, -17) * mm});
            skLineSegment(sketch, "E96.0.5.1", {"start": v(-12.5, -17) * mm, "end": v(-12.5, -19) * mm});
            skPoint(sketch, "E96.0.5.2", {"position": v(-13.5, -18) * mm});
            skLineSegment(sketch, "E96.0.5.3", {"start": v(-14.5, -19) * mm, "end": v(-12.5, -19) * mm});
            skLineSegment(sketch, "E96.0.5.4", {"start": v(-14.5, -17) * mm, "end": v(-14.5, -19) * mm});
            skLineSegment(sketch, "E96.0.6.0", {"start": v(-14.5, -13) * mm, "end": v(-12.5, -13) * mm});
            skLineSegment(sketch, "E96.0.6.1", {"start": v(-12.5, -13) * mm, "end": v(-12.5, -15) * mm});
            skPoint(sketch, "E96.0.6.2", {"position": v(-13.5, -14) * mm});
            skLineSegment(sketch, "E96.0.6.3", {"start": v(-14.5, -15) * mm, "end": v(-12.5, -15) * mm});
            skLineSegment(sketch, "E96.0.6.4", {"start": v(-14.5, -13) * mm, "end": v(-14.5, -15) * mm});
            skLineSegment(sketch, "E96.0.7.0", {"start": v(-14.5, -9) * mm, "end": v(-12.5, -9) * mm});
            skLineSegment(sketch, "E96.0.7.1", {"start": v(-12.5, -9) * mm, "end": v(-12.5, -11) * mm});
            skPoint(sketch, "E96.0.7.2", {"position": v(-13.5, -10) * mm});
            skLineSegment(sketch, "E96.0.7.3", {"start": v(-14.5, -11) * mm, "end": v(-12.5, -11) * mm});
            skLineSegment(sketch, "E96.0.7.4", {"start": v(-14.5, -9) * mm, "end": v(-14.5, -11) * mm});
            skLineSegment(sketch, "E96.1.0.0", {"start": v(-18.5, -37) * mm, "end": v(-16.5, -37) * mm});
            skLineSegment(sketch, "E96.1.0.1", {"start": v(-16.5, -37) * mm, "end": v(-16.5, -39) * mm});
            skPoint(sketch, "E96.1.0.2", {"position": v(-17.5, -38) * mm});
            skLineSegment(sketch, "E96.1.0.3", {"start": v(-18.5, -39) * mm, "end": v(-16.5, -39) * mm});
            skLineSegment(sketch, "E96.1.0.4", {"start": v(-18.5, -37) * mm, "end": v(-18.5, -39) * mm});
            skLineSegment(sketch, "E96.1.1.0", {"start": v(-18.5, -33) * mm, "end": v(-16.5, -33) * mm});
            skLineSegment(sketch, "E96.1.1.1", {"start": v(-16.5, -33) * mm, "end": v(-16.5, -35) * mm});
            skPoint(sketch, "E96.1.1.2", {"position": v(-17.5, -34) * mm});
            skLineSegment(sketch, "E96.1.1.3", {"start": v(-18.5, -35) * mm, "end": v(-16.5, -35) * mm});
            skLineSegment(sketch, "E96.1.1.4", {"start": v(-18.5, -33) * mm, "end": v(-18.5, -35) * mm});
            skLineSegment(sketch, "E96.1.2.0", {"start": v(-18.5, -29) * mm, "end": v(-16.5, -29) * mm});
            skLineSegment(sketch, "E96.1.2.1", {"start": v(-16.5, -29) * mm, "end": v(-16.5, -31) * mm});
            skPoint(sketch, "E96.1.2.2", {"position": v(-17.5, -30) * mm});
            skLineSegment(sketch, "E96.1.2.3", {"start": v(-18.5, -31) * mm, "end": v(-16.5, -31) * mm});
            skLineSegment(sketch, "E96.1.2.4", {"start": v(-18.5, -29) * mm, "end": v(-18.5, -31) * mm});
            skLineSegment(sketch, "E96.1.3.0", {"start": v(-18.5, -25) * mm, "end": v(-16.5, -25) * mm});
            skLineSegment(sketch, "E96.1.3.1", {"start": v(-16.5, -25) * mm, "end": v(-16.5, -27) * mm});
            skPoint(sketch, "E96.1.3.2", {"position": v(-17.5, -26) * mm});
            skLineSegment(sketch, "E96.1.3.3", {"start": v(-18.5, -27) * mm, "end": v(-16.5, -27) * mm});
            skLineSegment(sketch, "E96.1.3.4", {"start": v(-18.5, -25) * mm, "end": v(-18.5, -27) * mm});
            skLineSegment(sketch, "E96.1.4.0", {"start": v(-18.5, -21) * mm, "end": v(-16.5, -21) * mm});
            skLineSegment(sketch, "E96.1.4.1", {"start": v(-16.5, -21) * mm, "end": v(-16.5, -23) * mm});
            skPoint(sketch, "E96.1.4.2", {"position": v(-17.5, -22) * mm});
            skLineSegment(sketch, "E96.1.4.3", {"start": v(-18.5, -23) * mm, "end": v(-16.5, -23) * mm});
            skLineSegment(sketch, "E96.1.4.4", {"start": v(-18.5, -21) * mm, "end": v(-18.5, -23) * mm});
            skLineSegment(sketch, "E96.1.5.0", {"start": v(-18.5, -17) * mm, "end": v(-16.5, -17) * mm});
            skLineSegment(sketch, "E96.1.5.1", {"start": v(-16.5, -17) * mm, "end": v(-16.5, -19) * mm});
            skPoint(sketch, "E96.1.5.2", {"position": v(-17.5, -18) * mm});
            skLineSegment(sketch, "E96.1.5.3", {"start": v(-18.5, -19) * mm, "end": v(-16.5, -19) * mm});
            skLineSegment(sketch, "E96.1.5.4", {"start": v(-18.5, -17) * mm, "end": v(-18.5, -19) * mm});
            skLineSegment(sketch, "E96.1.6.0", {"start": v(-18.5, -13) * mm, "end": v(-16.5, -13) * mm});
            skLineSegment(sketch, "E96.1.6.1", {"start": v(-16.5, -13) * mm, "end": v(-16.5, -15) * mm});
            skPoint(sketch, "E96.1.6.2", {"position": v(-17.5, -14) * mm});
            skLineSegment(sketch, "E96.1.6.3", {"start": v(-18.5, -15) * mm, "end": v(-16.5, -15) * mm});
            skLineSegment(sketch, "E96.1.6.4", {"start": v(-18.5, -13) * mm, "end": v(-18.5, -15) * mm});
            skLineSegment(sketch, "E96.1.7.0", {"start": v(-18.5, -9) * mm, "end": v(-16.5, -9) * mm});
            skLineSegment(sketch, "E96.1.7.1", {"start": v(-16.5, -9) * mm, "end": v(-16.5, -11) * mm});
            skPoint(sketch, "E96.1.7.2", {"position": v(-17.5, -10) * mm});
            skLineSegment(sketch, "E96.1.7.3", {"start": v(-18.5, -11) * mm, "end": v(-16.5, -11) * mm});
            skLineSegment(sketch, "E96.1.7.4", {"start": v(-18.5, -9) * mm, "end": v(-18.5, -11) * mm});
            skLineSegment(sketch, "E96.2.0.0", {"start": v(-22.5, -37) * mm, "end": v(-20.5, -37) * mm});
            skLineSegment(sketch, "E96.2.0.1", {"start": v(-20.5, -37) * mm, "end": v(-20.5, -39) * mm});
            skPoint(sketch, "E96.2.0.2", {"position": v(-21.5, -38) * mm});
            skLineSegment(sketch, "E96.2.0.3", {"start": v(-22.5, -39) * mm, "end": v(-20.5, -39) * mm});
            skLineSegment(sketch, "E96.2.0.4", {"start": v(-22.5, -37) * mm, "end": v(-22.5, -39) * mm});
            skLineSegment(sketch, "E96.2.1.0", {"start": v(-22.5, -33) * mm, "end": v(-20.5, -33) * mm});
            skLineSegment(sketch, "E96.2.1.1", {"start": v(-20.5, -33) * mm, "end": v(-20.5, -35) * mm});
            skPoint(sketch, "E96.2.1.2", {"position": v(-21.5, -34) * mm});
            skLineSegment(sketch, "E96.2.1.3", {"start": v(-22.5, -35) * mm, "end": v(-20.5, -35) * mm});
            skLineSegment(sketch, "E96.2.1.4", {"start": v(-22.5, -33) * mm, "end": v(-22.5, -35) * mm});
            skLineSegment(sketch, "E96.2.2.0", {"start": v(-22.5, -29) * mm, "end": v(-20.5, -29) * mm});
            skLineSegment(sketch, "E96.2.2.1", {"start": v(-20.5, -29) * mm, "end": v(-20.5, -31) * mm});
            skPoint(sketch, "E96.2.2.2", {"position": v(-21.5, -30) * mm});
            skLineSegment(sketch, "E96.2.2.3", {"start": v(-22.5, -31) * mm, "end": v(-20.5, -31) * mm});
            skLineSegment(sketch, "E96.2.2.4", {"start": v(-22.5, -29) * mm, "end": v(-22.5, -31) * mm});
            skLineSegment(sketch, "E96.2.3.0", {"start": v(-22.5, -25) * mm, "end": v(-20.5, -25) * mm});
            skLineSegment(sketch, "E96.2.3.1", {"start": v(-20.5, -25) * mm, "end": v(-20.5, -27) * mm});
            skPoint(sketch, "E96.2.3.2", {"position": v(-21.5, -26) * mm});
            skLineSegment(sketch, "E96.2.3.3", {"start": v(-22.5, -27) * mm, "end": v(-20.5, -27) * mm});
            skLineSegment(sketch, "E96.2.3.4", {"start": v(-22.5, -25) * mm, "end": v(-22.5, -27) * mm});
            skLineSegment(sketch, "E96.2.4.0", {"start": v(-22.5, -21) * mm, "end": v(-20.5, -21) * mm});
            skLineSegment(sketch, "E96.2.4.1", {"start": v(-20.5, -21) * mm, "end": v(-20.5, -23) * mm});
            skPoint(sketch, "E96.2.4.2", {"position": v(-21.5, -22) * mm});
            skLineSegment(sketch, "E96.2.4.3", {"start": v(-22.5, -23) * mm, "end": v(-20.5, -23) * mm});
            skLineSegment(sketch, "E96.2.4.4", {"start": v(-22.5, -21) * mm, "end": v(-22.5, -23) * mm});
            skLineSegment(sketch, "E96.2.5.0", {"start": v(-22.5, -17) * mm, "end": v(-20.5, -17) * mm});
            skLineSegment(sketch, "E96.2.5.1", {"start": v(-20.5, -17) * mm, "end": v(-20.5, -19) * mm});
            skPoint(sketch, "E96.2.5.2", {"position": v(-21.5, -18) * mm});
            skLineSegment(sketch, "E96.2.5.3", {"start": v(-22.5, -19) * mm, "end": v(-20.5, -19) * mm});
            skLineSegment(sketch, "E96.2.5.4", {"start": v(-22.5, -17) * mm, "end": v(-22.5, -19) * mm});
            skLineSegment(sketch, "E96.2.6.0", {"start": v(-22.5, -13) * mm, "end": v(-20.5, -13) * mm});
            skLineSegment(sketch, "E96.2.6.1", {"start": v(-20.5, -13) * mm, "end": v(-20.5, -15) * mm});
            skPoint(sketch, "E96.2.6.2", {"position": v(-21.5, -14) * mm});
            skLineSegment(sketch, "E96.2.6.3", {"start": v(-22.5, -15) * mm, "end": v(-20.5, -15) * mm});
            skLineSegment(sketch, "E96.2.6.4", {"start": v(-22.5, -13) * mm, "end": v(-22.5, -15) * mm});
            skLineSegment(sketch, "E96.2.7.0", {"start": v(-22.5, -9) * mm, "end": v(-20.5, -9) * mm});
            skLineSegment(sketch, "E96.2.7.1", {"start": v(-20.5, -9) * mm, "end": v(-20.5, -11) * mm});
            skPoint(sketch, "E96.2.7.2", {"position": v(-21.5, -10) * mm});
            skLineSegment(sketch, "E96.2.7.3", {"start": v(-22.5, -11) * mm, "end": v(-20.5, -11) * mm});
            skLineSegment(sketch, "E96.2.7.4", {"start": v(-22.5, -9) * mm, "end": v(-22.5, -11) * mm});
            skLineSegment(sketch, "E96.3.0.0", {"start": v(-26.5, -37) * mm, "end": v(-24.5, -37) * mm});
            skLineSegment(sketch, "E96.3.0.1", {"start": v(-24.5, -37) * mm, "end": v(-24.5, -39) * mm});
            skPoint(sketch, "E96.3.0.2", {"position": v(-25.5, -38) * mm});
            skLineSegment(sketch, "E96.3.0.3", {"start": v(-26.5, -39) * mm, "end": v(-24.5, -39) * mm});
            skLineSegment(sketch, "E96.3.0.4", {"start": v(-26.5, -37) * mm, "end": v(-26.5, -39) * mm});
            skLineSegment(sketch, "E96.3.1.0", {"start": v(-26.5, -33) * mm, "end": v(-24.5, -33) * mm});
            skLineSegment(sketch, "E96.3.1.1", {"start": v(-24.5, -33) * mm, "end": v(-24.5, -35) * mm});
            skPoint(sketch, "E96.3.1.2", {"position": v(-25.5, -34) * mm});
            skLineSegment(sketch, "E96.3.1.3", {"start": v(-26.5, -35) * mm, "end": v(-24.5, -35) * mm});
            skLineSegment(sketch, "E96.3.1.4", {"start": v(-26.5, -33) * mm, "end": v(-26.5, -35) * mm});
            skLineSegment(sketch, "E96.3.2.0", {"start": v(-26.5, -29) * mm, "end": v(-24.5, -29) * mm});
            skLineSegment(sketch, "E96.3.2.1", {"start": v(-24.5, -29) * mm, "end": v(-24.5, -31) * mm});
            skPoint(sketch, "E96.3.2.2", {"position": v(-25.5, -30) * mm});
            skLineSegment(sketch, "E96.3.2.3", {"start": v(-26.5, -31) * mm, "end": v(-24.5, -31) * mm});
            skLineSegment(sketch, "E96.3.2.4", {"start": v(-26.5, -29) * mm, "end": v(-26.5, -31) * mm});
            skLineSegment(sketch, "E96.3.3.0", {"start": v(-26.5, -25) * mm, "end": v(-24.5, -25) * mm});
            skLineSegment(sketch, "E96.3.3.1", {"start": v(-24.5, -25) * mm, "end": v(-24.5, -27) * mm});
            skPoint(sketch, "E96.3.3.2", {"position": v(-25.5, -26) * mm});
            skLineSegment(sketch, "E96.3.3.3", {"start": v(-26.5, -27) * mm, "end": v(-24.5, -27) * mm});
            skLineSegment(sketch, "E96.3.3.4", {"start": v(-26.5, -25) * mm, "end": v(-26.5, -27) * mm});
            skLineSegment(sketch, "E96.3.4.0", {"start": v(-26.5, -21) * mm, "end": v(-24.5, -21) * mm});
            skLineSegment(sketch, "E96.3.4.1", {"start": v(-24.5, -21) * mm, "end": v(-24.5, -23) * mm});
            skPoint(sketch, "E96.3.4.2", {"position": v(-25.5, -22) * mm});
            skLineSegment(sketch, "E96.3.4.3", {"start": v(-26.5, -23) * mm, "end": v(-24.5, -23) * mm});
            skLineSegment(sketch, "E96.3.4.4", {"start": v(-26.5, -21) * mm, "end": v(-26.5, -23) * mm});
            skLineSegment(sketch, "E96.3.5.0", {"start": v(-26.5, -17) * mm, "end": v(-24.5, -17) * mm});
            skLineSegment(sketch, "E96.3.5.1", {"start": v(-24.5, -17) * mm, "end": v(-24.5, -19) * mm});
            skPoint(sketch, "E96.3.5.2", {"position": v(-25.5, -18) * mm});
            skLineSegment(sketch, "E96.3.5.3", {"start": v(-26.5, -19) * mm, "end": v(-24.5, -19) * mm});
            skLineSegment(sketch, "E96.3.5.4", {"start": v(-26.5, -17) * mm, "end": v(-26.5, -19) * mm});
            skLineSegment(sketch, "E96.3.6.0", {"start": v(-26.5, -13) * mm, "end": v(-24.5, -13) * mm});
            skLineSegment(sketch, "E96.3.6.1", {"start": v(-24.5, -13) * mm, "end": v(-24.5, -15) * mm});
            skPoint(sketch, "E96.3.6.2", {"position": v(-25.5, -14) * mm});
            skLineSegment(sketch, "E96.3.6.3", {"start": v(-26.5, -15) * mm, "end": v(-24.5, -15) * mm});
            skLineSegment(sketch, "E96.3.6.4", {"start": v(-26.5, -13) * mm, "end": v(-26.5, -15) * mm});
            skLineSegment(sketch, "E96.3.7.0", {"start": v(-26.5, -9) * mm, "end": v(-24.5, -9) * mm});
            skLineSegment(sketch, "E96.3.7.1", {"start": v(-24.5, -9) * mm, "end": v(-24.5, -11) * mm});
            skPoint(sketch, "E96.3.7.2", {"position": v(-25.5, -10) * mm});
            skLineSegment(sketch, "E96.3.7.3", {"start": v(-26.5, -11) * mm, "end": v(-24.5, -11) * mm});
            skLineSegment(sketch, "E96.3.7.4", {"start": v(-26.5, -9) * mm, "end": v(-26.5, -11) * mm});
            skLineSegment(sketch, "E96.4.0.0", {"start": v(-30.5, -37) * mm, "end": v(-28.5, -37) * mm});
            skLineSegment(sketch, "E96.4.0.1", {"start": v(-28.5, -37) * mm, "end": v(-28.5, -39) * mm});
            skPoint(sketch, "E96.4.0.2", {"position": v(-29.5, -38) * mm});
            skLineSegment(sketch, "E96.4.0.3", {"start": v(-30.5, -39) * mm, "end": v(-28.5, -39) * mm});
            skLineSegment(sketch, "E96.4.0.4", {"start": v(-30.5, -37) * mm, "end": v(-30.5, -39) * mm});
            skLineSegment(sketch, "E96.4.1.0", {"start": v(-30.5, -33) * mm, "end": v(-28.5, -33) * mm});
            skLineSegment(sketch, "E96.4.1.1", {"start": v(-28.5, -33) * mm, "end": v(-28.5, -35) * mm});
            skPoint(sketch, "E96.4.1.2", {"position": v(-29.5, -34) * mm});
            skLineSegment(sketch, "E96.4.1.3", {"start": v(-30.5, -35) * mm, "end": v(-28.5, -35) * mm});
            skLineSegment(sketch, "E96.4.1.4", {"start": v(-30.5, -33) * mm, "end": v(-30.5, -35) * mm});
            skLineSegment(sketch, "E96.4.2.0", {"start": v(-30.5, -29) * mm, "end": v(-28.5, -29) * mm});
            skLineSegment(sketch, "E96.4.2.1", {"start": v(-28.5, -29) * mm, "end": v(-28.5, -31) * mm});
            skPoint(sketch, "E96.4.2.2", {"position": v(-29.5, -30) * mm});
            skLineSegment(sketch, "E96.4.2.3", {"start": v(-30.5, -31) * mm, "end": v(-28.5, -31) * mm});
            skLineSegment(sketch, "E96.4.2.4", {"start": v(-30.5, -29) * mm, "end": v(-30.5, -31) * mm});
            skLineSegment(sketch, "E96.4.3.0", {"start": v(-30.5, -25) * mm, "end": v(-28.5, -25) * mm});
            skLineSegment(sketch, "E96.4.3.1", {"start": v(-28.5, -25) * mm, "end": v(-28.5, -27) * mm});
            skPoint(sketch, "E96.4.3.2", {"position": v(-29.5, -26) * mm});
            skLineSegment(sketch, "E96.4.3.3", {"start": v(-30.5, -27) * mm, "end": v(-28.5, -27) * mm});
            skLineSegment(sketch, "E96.4.3.4", {"start": v(-30.5, -25) * mm, "end": v(-30.5, -27) * mm});
            skLineSegment(sketch, "E96.4.4.0", {"start": v(-30.5, -21) * mm, "end": v(-28.5, -21) * mm});
            skLineSegment(sketch, "E96.4.4.1", {"start": v(-28.5, -21) * mm, "end": v(-28.5, -23) * mm});
            skPoint(sketch, "E96.4.4.2", {"position": v(-29.5, -22) * mm});
            skLineSegment(sketch, "E96.4.4.3", {"start": v(-30.5, -23) * mm, "end": v(-28.5, -23) * mm});
            skLineSegment(sketch, "E96.4.4.4", {"start": v(-30.5, -21) * mm, "end": v(-30.5, -23) * mm});
            skLineSegment(sketch, "E96.4.5.0", {"start": v(-30.5, -17) * mm, "end": v(-28.5, -17) * mm});
            skLineSegment(sketch, "E96.4.5.1", {"start": v(-28.5, -17) * mm, "end": v(-28.5, -19) * mm});
            skPoint(sketch, "E96.4.5.2", {"position": v(-29.5, -18) * mm});
            skLineSegment(sketch, "E96.4.5.3", {"start": v(-30.5, -19) * mm, "end": v(-28.5, -19) * mm});
            skLineSegment(sketch, "E96.4.5.4", {"start": v(-30.5, -17) * mm, "end": v(-30.5, -19) * mm});
            skLineSegment(sketch, "E96.4.6.0", {"start": v(-30.5, -13) * mm, "end": v(-28.5, -13) * mm});
            skLineSegment(sketch, "E96.4.6.1", {"start": v(-28.5, -13) * mm, "end": v(-28.5, -15) * mm});
            skPoint(sketch, "E96.4.6.2", {"position": v(-29.5, -14) * mm});
            skLineSegment(sketch, "E96.4.6.3", {"start": v(-30.5, -15) * mm, "end": v(-28.5, -15) * mm});
            skLineSegment(sketch, "E96.4.6.4", {"start": v(-30.5, -13) * mm, "end": v(-30.5, -15) * mm});
            skLineSegment(sketch, "E96.4.7.0", {"start": v(-30.5, -9) * mm, "end": v(-28.5, -9) * mm});
            skLineSegment(sketch, "E96.4.7.1", {"start": v(-28.5, -9) * mm, "end": v(-28.5, -11) * mm});
            skPoint(sketch, "E96.4.7.2", {"position": v(-29.5, -10) * mm});
            skLineSegment(sketch, "E96.4.7.3", {"start": v(-30.5, -11) * mm, "end": v(-28.5, -11) * mm});
            skLineSegment(sketch, "E96.4.7.4", {"start": v(-30.5, -9) * mm, "end": v(-30.5, -11) * mm});
            skLineSegment(sketch, "E96.5.0.0", {"start": v(-34.5, -37) * mm, "end": v(-32.5, -37) * mm});
            skLineSegment(sketch, "E96.5.0.1", {"start": v(-32.5, -37) * mm, "end": v(-32.5, -39) * mm});
            skPoint(sketch, "E96.5.0.2", {"position": v(-33.5, -38) * mm});
            skLineSegment(sketch, "E96.5.0.3", {"start": v(-34.5, -39) * mm, "end": v(-32.5, -39) * mm});
            skLineSegment(sketch, "E96.5.0.4", {"start": v(-34.5, -37) * mm, "end": v(-34.5, -39) * mm});
            skLineSegment(sketch, "E96.5.1.0", {"start": v(-34.5, -33) * mm, "end": v(-32.5, -33) * mm});
            skLineSegment(sketch, "E96.5.1.1", {"start": v(-32.5, -33) * mm, "end": v(-32.5, -35) * mm});
            skPoint(sketch, "E96.5.1.2", {"position": v(-33.5, -34) * mm});
            skLineSegment(sketch, "E96.5.1.3", {"start": v(-34.5, -35) * mm, "end": v(-32.5, -35) * mm});
            skLineSegment(sketch, "E96.5.1.4", {"start": v(-34.5, -33) * mm, "end": v(-34.5, -35) * mm});
            skLineSegment(sketch, "E96.5.2.0", {"start": v(-34.5, -29) * mm, "end": v(-32.5, -29) * mm});
            skLineSegment(sketch, "E96.5.2.1", {"start": v(-32.5, -29) * mm, "end": v(-32.5, -31) * mm});
            skPoint(sketch, "E96.5.2.2", {"position": v(-33.5, -30) * mm});
            skLineSegment(sketch, "E96.5.2.3", {"start": v(-34.5, -31) * mm, "end": v(-32.5, -31) * mm});
            skLineSegment(sketch, "E96.5.2.4", {"start": v(-34.5, -29) * mm, "end": v(-34.5, -31) * mm});
            skLineSegment(sketch, "E96.5.3.0", {"start": v(-34.5, -25) * mm, "end": v(-32.5, -25) * mm});
            skLineSegment(sketch, "E96.5.3.1", {"start": v(-32.5, -25) * mm, "end": v(-32.5, -27) * mm});
            skPoint(sketch, "E96.5.3.2", {"position": v(-33.5, -26) * mm});
            skLineSegment(sketch, "E96.5.3.3", {"start": v(-34.5, -27) * mm, "end": v(-32.5, -27) * mm});
            skLineSegment(sketch, "E96.5.3.4", {"start": v(-34.5, -25) * mm, "end": v(-34.5, -27) * mm});
            skLineSegment(sketch, "E96.5.4.0", {"start": v(-34.5, -21) * mm, "end": v(-32.5, -21) * mm});
            skLineSegment(sketch, "E96.5.4.1", {"start": v(-32.5, -21) * mm, "end": v(-32.5, -23) * mm});
            skPoint(sketch, "E96.5.4.2", {"position": v(-33.5, -22) * mm});
            skLineSegment(sketch, "E96.5.4.3", {"start": v(-34.5, -23) * mm, "end": v(-32.5, -23) * mm});
            skLineSegment(sketch, "E96.5.4.4", {"start": v(-34.5, -21) * mm, "end": v(-34.5, -23) * mm});
            skLineSegment(sketch, "E96.5.5.0", {"start": v(-34.5, -17) * mm, "end": v(-32.5, -17) * mm});
            skLineSegment(sketch, "E96.5.5.1", {"start": v(-32.5, -17) * mm, "end": v(-32.5, -19) * mm});
            skPoint(sketch, "E96.5.5.2", {"position": v(-33.5, -18) * mm});
            skLineSegment(sketch, "E96.5.5.3", {"start": v(-34.5, -19) * mm, "end": v(-32.5, -19) * mm});
            skLineSegment(sketch, "E96.5.5.4", {"start": v(-34.5, -17) * mm, "end": v(-34.5, -19) * mm});
            skLineSegment(sketch, "E96.5.6.0", {"start": v(-34.5, -13) * mm, "end": v(-32.5, -13) * mm});
            skLineSegment(sketch, "E96.5.6.1", {"start": v(-32.5, -13) * mm, "end": v(-32.5, -15) * mm});
            skPoint(sketch, "E96.5.6.2", {"position": v(-33.5, -14) * mm});
            skLineSegment(sketch, "E96.5.6.3", {"start": v(-34.5, -15) * mm, "end": v(-32.5, -15) * mm});
            skLineSegment(sketch, "E96.5.6.4", {"start": v(-34.5, -13) * mm, "end": v(-34.5, -15) * mm});
            skLineSegment(sketch, "E96.5.7.0", {"start": v(-34.5, -9) * mm, "end": v(-32.5, -9) * mm});
            skLineSegment(sketch, "E96.5.7.1", {"start": v(-32.5, -9) * mm, "end": v(-32.5, -11) * mm});
            skPoint(sketch, "E96.5.7.2", {"position": v(-33.5, -10) * mm});
            skLineSegment(sketch, "E96.5.7.3", {"start": v(-34.5, -11) * mm, "end": v(-32.5, -11) * mm});
            skLineSegment(sketch, "E96.5.7.4", {"start": v(-34.5, -9) * mm, "end": v(-34.5, -11) * mm});
            skLineSegment(sketch, "E96.6.0.0", {"start": v(-38.5, -37) * mm, "end": v(-36.5, -37) * mm});
            skLineSegment(sketch, "E96.6.0.1", {"start": v(-36.5, -37) * mm, "end": v(-36.5, -39) * mm});
            skPoint(sketch, "E96.6.0.2", {"position": v(-37.5, -38) * mm});
            skLineSegment(sketch, "E96.6.0.3", {"start": v(-38.5, -39) * mm, "end": v(-36.5, -39) * mm});
            skLineSegment(sketch, "E96.6.0.4", {"start": v(-38.5, -37) * mm, "end": v(-38.5, -39) * mm});
            skLineSegment(sketch, "E96.6.1.0", {"start": v(-38.5, -33) * mm, "end": v(-36.5, -33) * mm});
            skLineSegment(sketch, "E96.6.1.1", {"start": v(-36.5, -33) * mm, "end": v(-36.5, -35) * mm});
            skPoint(sketch, "E96.6.1.2", {"position": v(-37.5, -34) * mm});
            skLineSegment(sketch, "E96.6.1.3", {"start": v(-38.5, -35) * mm, "end": v(-36.5, -35) * mm});
            skLineSegment(sketch, "E96.6.1.4", {"start": v(-38.5, -33) * mm, "end": v(-38.5, -35) * mm});
            skLineSegment(sketch, "E96.6.2.0", {"start": v(-38.5, -29) * mm, "end": v(-36.5, -29) * mm});
            skLineSegment(sketch, "E96.6.2.1", {"start": v(-36.5, -29) * mm, "end": v(-36.5, -31) * mm});
            skPoint(sketch, "E96.6.2.2", {"position": v(-37.5, -30) * mm});
            skLineSegment(sketch, "E96.6.2.3", {"start": v(-38.5, -31) * mm, "end": v(-36.5, -31) * mm});
            skLineSegment(sketch, "E96.6.2.4", {"start": v(-38.5, -29) * mm, "end": v(-38.5, -31) * mm});
            skLineSegment(sketch, "E96.6.3.0", {"start": v(-38.5, -25) * mm, "end": v(-36.5, -25) * mm});
            skLineSegment(sketch, "E96.6.3.1", {"start": v(-36.5, -25) * mm, "end": v(-36.5, -27) * mm});
            skPoint(sketch, "E96.6.3.2", {"position": v(-37.5, -26) * mm});
            skLineSegment(sketch, "E96.6.3.3", {"start": v(-38.5, -27) * mm, "end": v(-36.5, -27) * mm});
            skLineSegment(sketch, "E96.6.3.4", {"start": v(-38.5, -25) * mm, "end": v(-38.5, -27) * mm});
            skLineSegment(sketch, "E96.6.4.0", {"start": v(-38.5, -21) * mm, "end": v(-36.5, -21) * mm});
            skLineSegment(sketch, "E96.6.4.1", {"start": v(-36.5, -21) * mm, "end": v(-36.5, -23) * mm});
            skPoint(sketch, "E96.6.4.2", {"position": v(-37.5, -22) * mm});
            skLineSegment(sketch, "E96.6.4.3", {"start": v(-38.5, -23) * mm, "end": v(-36.5, -23) * mm});
            skLineSegment(sketch, "E96.6.4.4", {"start": v(-38.5, -21) * mm, "end": v(-38.5, -23) * mm});
            skLineSegment(sketch, "E96.6.5.0", {"start": v(-38.5, -17) * mm, "end": v(-36.5, -17) * mm});
            skLineSegment(sketch, "E96.6.5.1", {"start": v(-36.5, -17) * mm, "end": v(-36.5, -19) * mm});
            skPoint(sketch, "E96.6.5.2", {"position": v(-37.5, -18) * mm});
            skLineSegment(sketch, "E96.6.5.3", {"start": v(-38.5, -19) * mm, "end": v(-36.5, -19) * mm});
            skLineSegment(sketch, "E96.6.5.4", {"start": v(-38.5, -17) * mm, "end": v(-38.5, -19) * mm});
            skLineSegment(sketch, "E96.6.6.0", {"start": v(-38.5, -13) * mm, "end": v(-36.5, -13) * mm});
            skLineSegment(sketch, "E96.6.6.1", {"start": v(-36.5, -13) * mm, "end": v(-36.5, -15) * mm});
            skPoint(sketch, "E96.6.6.2", {"position": v(-37.5, -14) * mm});
            skLineSegment(sketch, "E96.6.6.3", {"start": v(-38.5, -15) * mm, "end": v(-36.5, -15) * mm});
            skLineSegment(sketch, "E96.6.6.4", {"start": v(-38.5, -13) * mm, "end": v(-38.5, -15) * mm});
            skLineSegment(sketch, "E96.6.7.0", {"start": v(-38.5, -9) * mm, "end": v(-36.5, -9) * mm});
            skLineSegment(sketch, "E96.6.7.1", {"start": v(-36.5, -9) * mm, "end": v(-36.5, -11) * mm});
            skPoint(sketch, "E96.6.7.2", {"position": v(-37.5, -10) * mm});
            skLineSegment(sketch, "E96.6.7.3", {"start": v(-38.5, -11) * mm, "end": v(-36.5, -11) * mm});
            skLineSegment(sketch, "E96.6.7.4", {"start": v(-38.5, -9) * mm, "end": v(-38.5, -11) * mm});
            skLineSegment(sketch, "E96.7.0.0", {"start": v(-42.5, -37) * mm, "end": v(-40.5, -37) * mm});
            skLineSegment(sketch, "E96.7.0.1", {"start": v(-40.5, -37) * mm, "end": v(-40.5, -39) * mm});
            skPoint(sketch, "E96.7.0.2", {"position": v(-41.5, -38) * mm});
            skLineSegment(sketch, "E96.7.0.3", {"start": v(-42.5, -39) * mm, "end": v(-40.5, -39) * mm});
            skLineSegment(sketch, "E96.7.0.4", {"start": v(-42.5, -37) * mm, "end": v(-42.5, -39) * mm});
            skLineSegment(sketch, "E96.7.1.0", {"start": v(-42.5, -33) * mm, "end": v(-40.5, -33) * mm});
            skLineSegment(sketch, "E96.7.1.1", {"start": v(-40.5, -33) * mm, "end": v(-40.5, -35) * mm});
            skPoint(sketch, "E96.7.1.2", {"position": v(-41.5, -34) * mm});
            skLineSegment(sketch, "E96.7.1.3", {"start": v(-42.5, -35) * mm, "end": v(-40.5, -35) * mm});
            skLineSegment(sketch, "E96.7.1.4", {"start": v(-42.5, -33) * mm, "end": v(-42.5, -35) * mm});
            skLineSegment(sketch, "E96.7.2.0", {"start": v(-42.5, -29) * mm, "end": v(-40.5, -29) * mm});
            skLineSegment(sketch, "E96.7.2.1", {"start": v(-40.5, -29) * mm, "end": v(-40.5, -31) * mm});
            skPoint(sketch, "E96.7.2.2", {"position": v(-41.5, -30) * mm});
            skLineSegment(sketch, "E96.7.2.3", {"start": v(-42.5, -31) * mm, "end": v(-40.5, -31) * mm});
            skLineSegment(sketch, "E96.7.2.4", {"start": v(-42.5, -29) * mm, "end": v(-42.5, -31) * mm});
            skLineSegment(sketch, "E96.7.3.0", {"start": v(-42.5, -25) * mm, "end": v(-40.5, -25) * mm});
            skLineSegment(sketch, "E96.7.3.1", {"start": v(-40.5, -25) * mm, "end": v(-40.5, -27) * mm});
            skPoint(sketch, "E96.7.3.2", {"position": v(-41.5, -26) * mm});
            skLineSegment(sketch, "E96.7.3.3", {"start": v(-42.5, -27) * mm, "end": v(-40.5, -27) * mm});
            skLineSegment(sketch, "E96.7.3.4", {"start": v(-42.5, -25) * mm, "end": v(-42.5, -27) * mm});
            skLineSegment(sketch, "E96.7.4.0", {"start": v(-42.5, -21) * mm, "end": v(-40.5, -21) * mm});
            skLineSegment(sketch, "E96.7.4.1", {"start": v(-40.5, -21) * mm, "end": v(-40.5, -23) * mm});
            skPoint(sketch, "E96.7.4.2", {"position": v(-41.5, -22) * mm});
            skLineSegment(sketch, "E96.7.4.3", {"start": v(-42.5, -23) * mm, "end": v(-40.5, -23) * mm});
            skLineSegment(sketch, "E96.7.4.4", {"start": v(-42.5, -21) * mm, "end": v(-42.5, -23) * mm});
            skLineSegment(sketch, "E96.7.5.0", {"start": v(-42.5, -17) * mm, "end": v(-40.5, -17) * mm});
            skLineSegment(sketch, "E96.7.5.1", {"start": v(-40.5, -17) * mm, "end": v(-40.5, -19) * mm});
            skPoint(sketch, "E96.7.5.2", {"position": v(-41.5, -18) * mm});
            skLineSegment(sketch, "E96.7.5.3", {"start": v(-42.5, -19) * mm, "end": v(-40.5, -19) * mm});
            skLineSegment(sketch, "E96.7.5.4", {"start": v(-42.5, -17) * mm, "end": v(-42.5, -19) * mm});
            skLineSegment(sketch, "E96.7.6.0", {"start": v(-42.5, -13) * mm, "end": v(-40.5, -13) * mm});
            skLineSegment(sketch, "E96.7.6.1", {"start": v(-40.5, -13) * mm, "end": v(-40.5, -15) * mm});
            skPoint(sketch, "E96.7.6.2", {"position": v(-41.5, -14) * mm});
            skLineSegment(sketch, "E96.7.6.3", {"start": v(-42.5, -15) * mm, "end": v(-40.5, -15) * mm});
            skLineSegment(sketch, "E96.7.6.4", {"start": v(-42.5, -13) * mm, "end": v(-42.5, -15) * mm});
            skLineSegment(sketch, "E96.7.7.0", {"start": v(-42.5, -9) * mm, "end": v(-40.5, -9) * mm});
            skLineSegment(sketch, "E96.7.7.1", {"start": v(-40.5, -9) * mm, "end": v(-40.5, -11) * mm});
            skPoint(sketch, "E96.7.7.2", {"position": v(-41.5, -10) * mm});
            skLineSegment(sketch, "E96.7.7.3", {"start": v(-42.5, -11) * mm, "end": v(-40.5, -11) * mm});
            skLineSegment(sketch, "E96.7.7.4", {"start": v(-42.5, -9) * mm, "end": v(-42.5, -11) * mm});
            skLineSegment(sketch, "E96.8.0.0", {"start": v(-46.5, -37) * mm, "end": v(-44.5, -37) * mm});
            skLineSegment(sketch, "E96.8.0.1", {"start": v(-44.5, -37) * mm, "end": v(-44.5, -39) * mm});
            skPoint(sketch, "E96.8.0.2", {"position": v(-45.5, -38) * mm});
            skLineSegment(sketch, "E96.8.0.3", {"start": v(-46.5, -39) * mm, "end": v(-44.5, -39) * mm});
            skLineSegment(sketch, "E96.8.0.4", {"start": v(-46.5, -37) * mm, "end": v(-46.5, -39) * mm});
            skLineSegment(sketch, "E96.8.1.0", {"start": v(-46.5, -33) * mm, "end": v(-44.5, -33) * mm});
            skLineSegment(sketch, "E96.8.1.1", {"start": v(-44.5, -33) * mm, "end": v(-44.5, -35) * mm});
            skPoint(sketch, "E96.8.1.2", {"position": v(-45.5, -34) * mm});
            skLineSegment(sketch, "E96.8.1.3", {"start": v(-46.5, -35) * mm, "end": v(-44.5, -35) * mm});
            skLineSegment(sketch, "E96.8.1.4", {"start": v(-46.5, -33) * mm, "end": v(-46.5, -35) * mm});
            skLineSegment(sketch, "E96.8.2.0", {"start": v(-46.5, -29) * mm, "end": v(-44.5, -29) * mm});
            skLineSegment(sketch, "E96.8.2.1", {"start": v(-44.5, -29) * mm, "end": v(-44.5, -31) * mm});
            skPoint(sketch, "E96.8.2.2", {"position": v(-45.5, -30) * mm});
            skLineSegment(sketch, "E96.8.2.3", {"start": v(-46.5, -31) * mm, "end": v(-44.5, -31) * mm});
            skLineSegment(sketch, "E96.8.2.4", {"start": v(-46.5, -29) * mm, "end": v(-46.5, -31) * mm});
            skLineSegment(sketch, "E96.8.3.0", {"start": v(-46.5, -25) * mm, "end": v(-44.5, -25) * mm});
            skLineSegment(sketch, "E96.8.3.1", {"start": v(-44.5, -25) * mm, "end": v(-44.5, -27) * mm});
            skPoint(sketch, "E96.8.3.2", {"position": v(-45.5, -26) * mm});
            skLineSegment(sketch, "E96.8.3.3", {"start": v(-46.5, -27) * mm, "end": v(-44.5, -27) * mm});
            skLineSegment(sketch, "E96.8.3.4", {"start": v(-46.5, -25) * mm, "end": v(-46.5, -27) * mm});
            skLineSegment(sketch, "E96.8.4.0", {"start": v(-46.5, -21) * mm, "end": v(-44.5, -21) * mm});
            skLineSegment(sketch, "E96.8.4.1", {"start": v(-44.5, -21) * mm, "end": v(-44.5, -23) * mm});
            skPoint(sketch, "E96.8.4.2", {"position": v(-45.5, -22) * mm});
            skLineSegment(sketch, "E96.8.4.3", {"start": v(-46.5, -23) * mm, "end": v(-44.5, -23) * mm});
            skLineSegment(sketch, "E96.8.4.4", {"start": v(-46.5, -21) * mm, "end": v(-46.5, -23) * mm});
            skLineSegment(sketch, "E96.8.5.0", {"start": v(-46.5, -17) * mm, "end": v(-44.5, -17) * mm});
            skLineSegment(sketch, "E96.8.5.1", {"start": v(-44.5, -17) * mm, "end": v(-44.5, -19) * mm});
            skPoint(sketch, "E96.8.5.2", {"position": v(-45.5, -18) * mm});
            skLineSegment(sketch, "E96.8.5.3", {"start": v(-46.5, -19) * mm, "end": v(-44.5, -19) * mm});
            skLineSegment(sketch, "E96.8.5.4", {"start": v(-46.5, -17) * mm, "end": v(-46.5, -19) * mm});
            skLineSegment(sketch, "E96.8.6.0", {"start": v(-46.5, -13) * mm, "end": v(-44.5, -13) * mm});
            skLineSegment(sketch, "E96.8.6.1", {"start": v(-44.5, -13) * mm, "end": v(-44.5, -15) * mm});
            skPoint(sketch, "E96.8.6.2", {"position": v(-45.5, -14) * mm});
            skLineSegment(sketch, "E96.8.6.3", {"start": v(-46.5, -15) * mm, "end": v(-44.5, -15) * mm});
            skLineSegment(sketch, "E96.8.6.4", {"start": v(-46.5, -13) * mm, "end": v(-46.5, -15) * mm});
            skLineSegment(sketch, "E96.8.7.0", {"start": v(-46.5, -9) * mm, "end": v(-44.5, -9) * mm});
            skLineSegment(sketch, "E96.8.7.1", {"start": v(-44.5, -9) * mm, "end": v(-44.5, -11) * mm});
            skPoint(sketch, "E96.8.7.2", {"position": v(-45.5, -10) * mm});
            skLineSegment(sketch, "E96.8.7.3", {"start": v(-46.5, -11) * mm, "end": v(-44.5, -11) * mm});
            skLineSegment(sketch, "E96.8.7.4", {"start": v(-46.5, -9) * mm, "end": v(-46.5, -11) * mm});
            skLineSegment(sketch, "E96.direction1", {"start": v(-14, -40.5) * mm, "end": v(-18, -40.5) * mm, "construction": true});
            skLineSegment(sketch, "E96.direction2", {"start": v(-14, -40.5) * mm, "end": v(-14, -36.5) * mm, "construction": true});
            skSolve(sketch);
        }
        {
            var Q0;
            Q0 = qSketchRegion(id + "F21", true);
            extrude(context, id + "F22", {"entities" : qUnion([Q0]), "operationType" : NewBodyOperationType.REMOVE, "oppositeDirection" : true, "depth" : 25 * mm, "offsetDistance" : 25 * mm});
        }
    });
